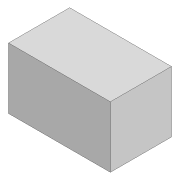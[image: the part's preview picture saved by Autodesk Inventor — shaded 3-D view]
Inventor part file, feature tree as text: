
AUTODESK INVENTOR PART (.ipt)
format: ipt  version: 2022 (Build 260153000, 153)  size: 74,752 bytes
history: native  units: mm
features: extrude x1, sketch x1
ambient origin geometry x8: Origin, YZ Plane, XZ Plane, XY Plane, X Axis, Y Axis, Z Axis, Center Point
bodies: Solid1 (feature_tree)
feature tree (2):
  extrude  "Extrusion1"  Depth=3.0mm
  sketch  "Sketch1"  dims[d0=5.0mm d1=3.0mm d2=3.0mm d3=0.0mm]
